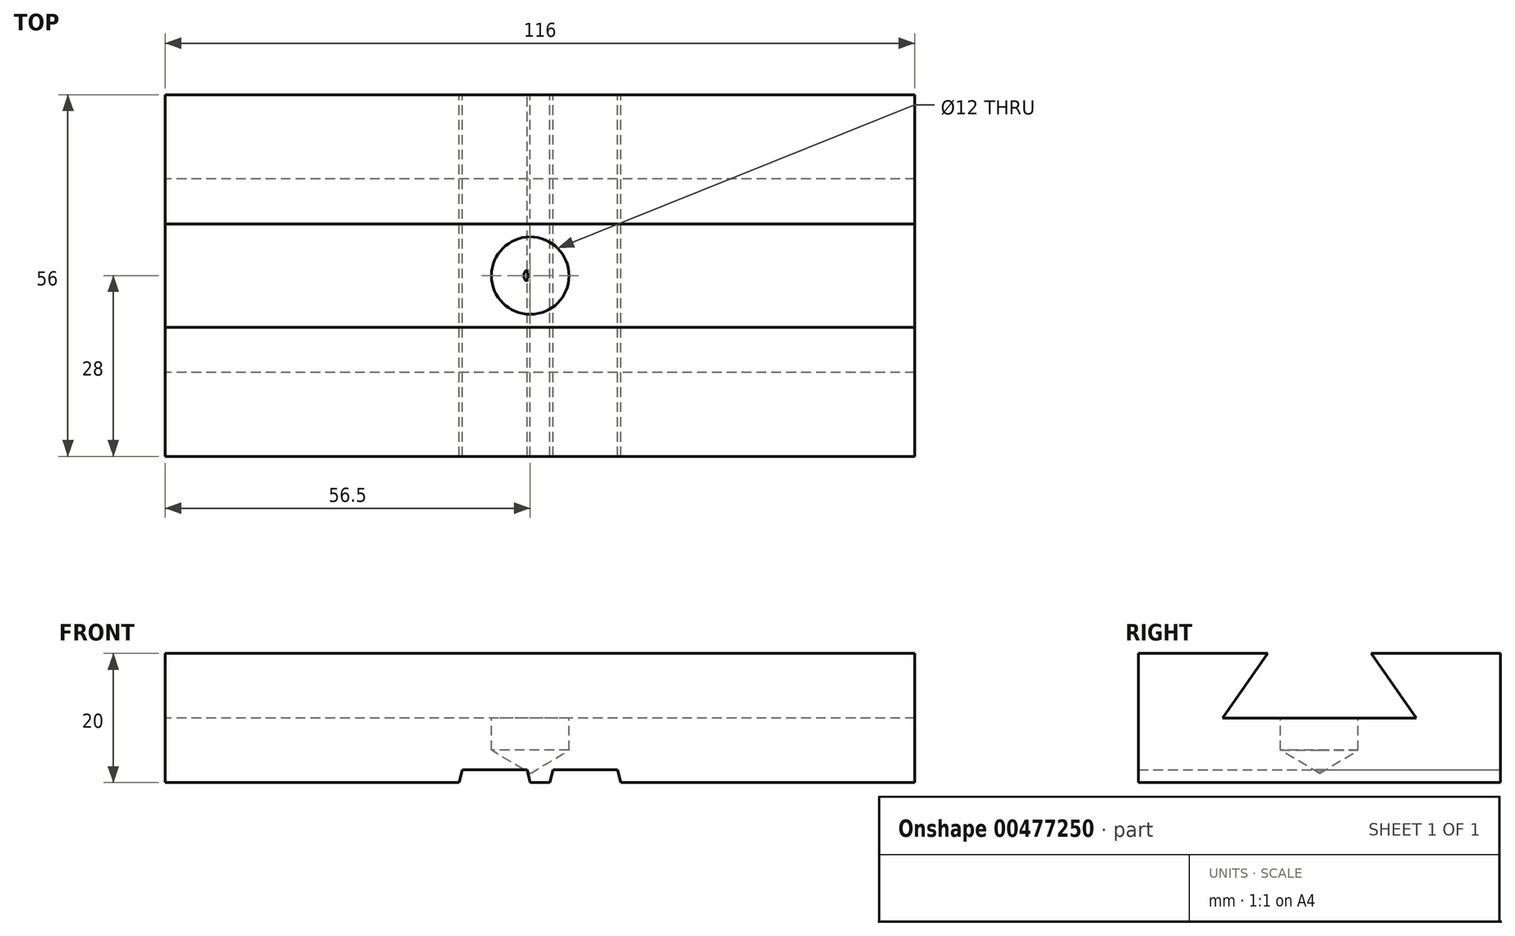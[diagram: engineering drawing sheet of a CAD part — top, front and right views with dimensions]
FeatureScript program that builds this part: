
annotation { "Feature Type Name" : "Feature", "Feature Type Description" : "" }
export const myFeature = defineFeature(function(context is Context, id is Id, definition is map)
    precondition{}
    {
        {
            var Q0;
            Q0=qCreatedBy(makeId("Front.planeOp"),FACE);
            var sketch = newSketch(context, id + "F0", { "sketchPlane" : qUnion([Q0])});
            skLineSegment(sketch, "E0", {"start": v(2, 2) * mm, "end": v(12, 2) * mm});
            skLineSegment(sketch, "E1", {"start": v(12, 2) * mm, "end": v(12.5, 0) * mm});
            skLineSegment(sketch, "E2", {"start": v(12.5, 0) * mm, "end": v(58, 0) * mm});
            skLineSegment(sketch, "E3", {"start": v(58, 0) * mm, "end": v(58, 20) * mm});
            skLineSegment(sketch, "E4", {"start": v(-58, 20) * mm, "end": v(-58, 0) * mm});
            skLineSegment(sketch, "E5", {"start": v(-58, 0) * mm, "end": v(-12.5, 0) * mm});
            skLineSegment(sketch, "E6", {"start": v(-12.5, 0) * mm, "end": v(-12, 2) * mm});
            skLineSegment(sketch, "E7", {"start": v(-12, 2) * mm, "end": v(-2, 2) * mm});
            skLineSegment(sketch, "E8", {"start": v(-58, 20) * mm, "end": v(58, 20) * mm});
            skLineSegment(sketch, "E9", {"start": v(0, 0) * mm, "end": v(-1.5, 0) * mm});
            skLineSegment(sketch, "E10", {"start": v(-1.5, 0) * mm, "end": v(-2, 2) * mm});
            skLineSegment(sketch, "E11", {"start": v(0, 0) * mm, "end": v(1.5, 0) * mm});
            skLineSegment(sketch, "E12", {"start": v(1.5, 0) * mm, "end": v(2, 2) * mm});
            skSolve(sketch);
        }
        {
            var Q0;
            Q0=makeQuery(id+"F0.imprint","IMPRINT",FACE,{"disambiguationData":[TD([[makeQuery(id+"F0.imprint","IMPRINT",EDGE,{"derivedFrom":sQuery(id+"F0.wireOp",EDGE,"zo6ZiONU-3IiS-W8wq-WPRh-nkQJYUhjSfGB")}),1.0]])]});
            var Q1;
            Q1=makeQuery(id+"F0.imprint","IMPRINT",FACE,{"disambiguationData":[TD([[makeQuery(id+"F0.imprint","IMPRINT",EDGE,{"derivedFrom":sQuery(id+"F0.wireOp",EDGE,"E0")}),1.0]])]});
            extrude(context, id + "F1", {"entities" : qUnion([Q0, Q1]), "depth" : 56 * mm});
        }
        {
            var Q0;
            Q0=makeQuery(id+"F1.opExtrude","SWEPT_FACE",FACE,{"disambiguationData":[OSD([sQuery(id+"F0.wireOp",EDGE,"E4")])]});
            var sketch = newSketch(context, id + "F2", { "sketchPlane" : qUnion([Q0])});
            skLineSegment(sketch, "E13", {"start": v(0, 20) * mm, "end": v(28, 20) * mm});
            skLineSegment(sketch, "E14", {"start": v(28, 20) * mm, "end": v(28, 10) * mm});
            skLineSegment(sketch, "E15", {"start": v(28, 10) * mm, "end": v(43, 10) * mm});
            skLineSegment(sketch, "E16", {"start": v(43, 10) * mm, "end": v(36, 20) * mm});
            skLineSegment(sketch, "E17", {"start": v(28, 10) * mm, "end": v(13, 10) * mm});
            skLineSegment(sketch, "E18", {"start": v(13, 10) * mm, "end": v(20, 20) * mm});
            skLineSegment(sketch, "E19", {"start": v(36, 20) * mm, "end": v(20, 20) * mm});
            skSolve(sketch);
        }
        {
            var Q0;
            {var subQ0=sQuery(id+"F2.wireOp",EDGE,"E14");Q0=makeQuery(id+"F2.imprint","IMPRINT",FACE,{"disambiguationData":[TD([[makeQuery(id+"F2.imprint","IMPRINT",EDGE,{"derivedFrom":subQ0}),-1.0]])]});}
            var Q1;
            {var subQ0=sQuery(id+"F2.wireOp",EDGE,"E14");Q1=makeQuery(id+"F2.imprint","IMPRINT",FACE,{"disambiguationData":[TD([[makeQuery(id+"F2.imprint","IMPRINT",EDGE,{"derivedFrom":subQ0}),1.0]])]});}
            extrude(context, id + "F3", {"entities" : qUnion([Q0, Q1]), "operationType" : NewBodyOperationType.REMOVE, "endBound" : BoundingType.UP_TO_NEXT, "oppositeDirection" : true, "depth" : 25 * mm});
        }
        {
            var Q0;
            Q0=makeQuery(id+"F3.boolean.opBoolean","COPY",FACE,{"derivedFrom":makeQuery(id+"F3.opExtrude","SWEPT_FACE",FACE,{"disambiguationData":[OSD([sQuery(id+"F2.wireOp",EDGE,"E15"),sQuery(id+"F2.wireOp",EDGE,"E17")])]})});
            var sketch = newSketch(context, id + "F4", { "sketchPlane" : qUnion([Q0])});
            skPoint(sketch, "E20", {"position": v(-1.5, -28) * mm});
            skSolve(sketch);
        }
        {
            var Q0;
            Q0=sQuery(id+"F4.wireOp",VERTEX,"E20");
            var Q1;
            Q1=makeQuery(id+"F1.opExtrude","SWEPT_BODY",BODY,{"disambiguationData":[OSD([sQuery(id+"F0.wireOp",EDGE,"E0"),sQuery(id+"F0.wireOp",EDGE,"E1"),sQuery(id+"F0.wireOp",EDGE,"E2"),sQuery(id+"F0.wireOp",EDGE,"E3"),sQuery(id+"F0.wireOp",EDGE,"E4"),sQuery(id+"F0.wireOp",EDGE,"E5"),sQuery(id+"F0.wireOp",EDGE,"E6"),sQuery(id+"F0.wireOp",EDGE,"E7"),sQuery(id+"F0.wireOp",EDGE,"E8"),sQuery(id+"F0.wireOp",EDGE,"E9"),sQuery(id+"F0.wireOp",EDGE,"E10"),sQuery(id+"F0.wireOp",EDGE,"E11"),sQuery(id+"F0.wireOp",EDGE,"E12")])]});
            hole(context, id + "F5", {"style" : HoleStyle.SIMPLE, "endStyle" : HoleEndStyle.BLIND, "holeDiameter" : 12 * mm, "holeDepth" : 5 * mm, "isTappedThrough" : true, "tappedDepth" : 12 * mm, "tapClearance" : 3, "locations" : qUnion([Q0]), "scope" : qUnion([Q1])});
        }
    });
